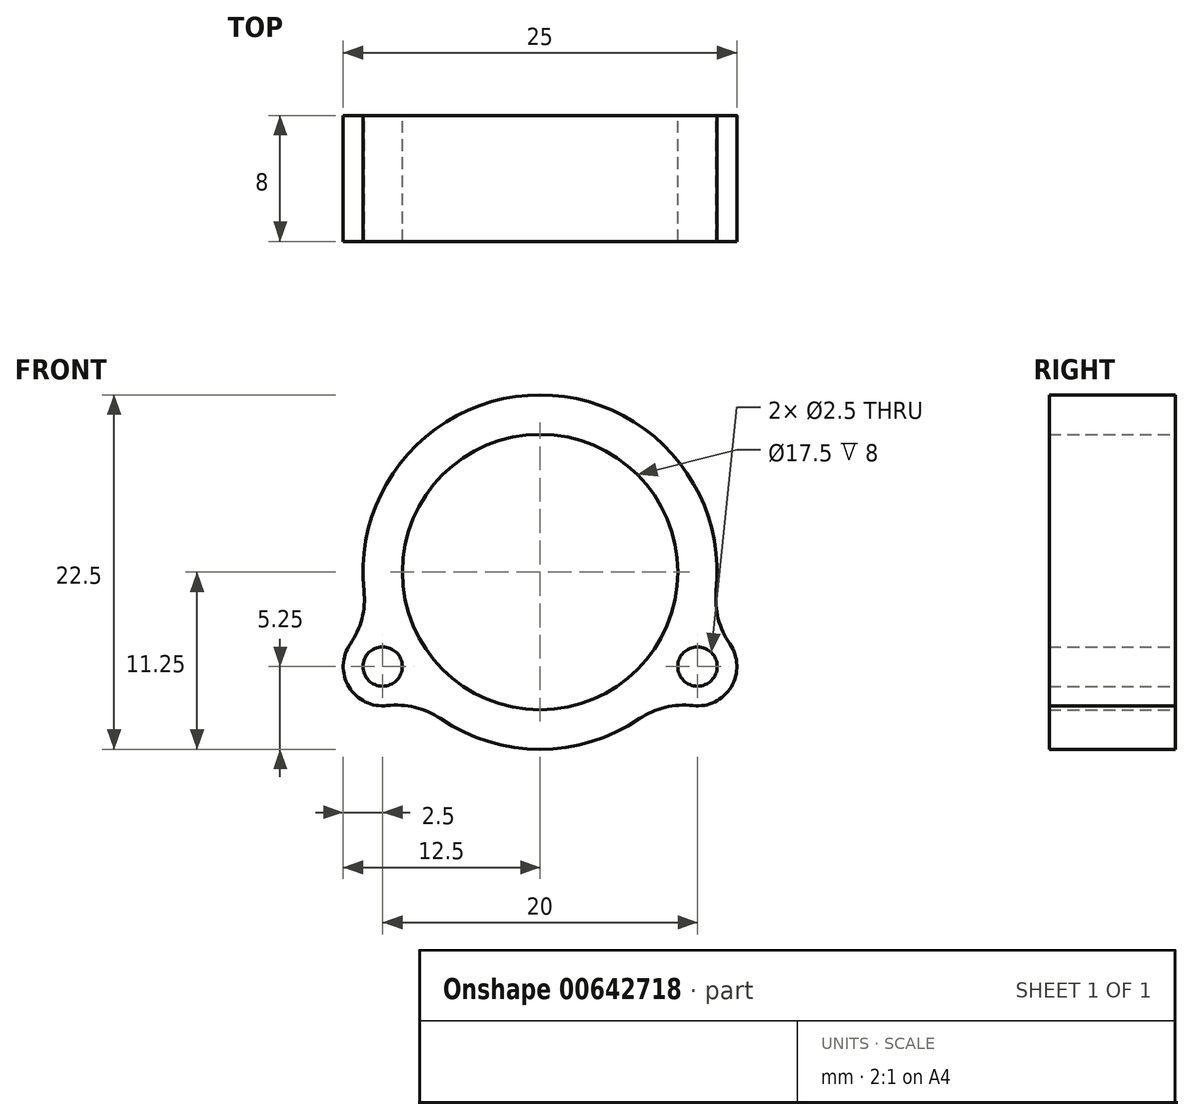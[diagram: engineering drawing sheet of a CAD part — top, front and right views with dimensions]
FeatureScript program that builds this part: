
annotation { "Feature Type Name" : "Feature", "Feature Type Description" : "" }
export const myFeature = defineFeature(function(context is Context, id is Id, definition is map)
    precondition{}
    {
        {
            var Q0;
            Q0=qCreatedBy(makeId("Front.planeOp"),FACE);
            var sketch = newSketch(context, id + "F0", { "sketchPlane" : qUnion([Q0])});
            skCircle(sketch, "E0", {"center": v(0, 0) * mm, "radius": 8.75 * mm});
            skArc(sketch, "E1", {"start": v(9.7, -8.48) * mm, "mid": v(12.14, -7.29) * mm, "end": v(12.05, -4.57) * mm});
            skArc(sketch, "E2", {"start": v(-12.05, -4.57) * mm, "mid": v(-12.14, -7.29) * mm, "end": v(-9.7, -8.48) * mm});
            skPoint(sketch, "E3.orphan", {"position": v(9, -6) * mm});
            skPoint(sketch, "E4.orphan", {"position": v(-11.68, -0.75) * mm});
            skPoint(sketch, "E5.start.orphan", {"position": v(-6.37, -6) * mm});
            skArc(sketch, "E6.trimOffspring", {"start": v(-6.31, -9.31) * mm, "mid": v(0, -11.25) * mm, "end": v(6.31, -9.31) * mm});
            skArc(sketch, "E7.trimOffspring", {"start": v(11.19, -1.2) * mm, "mid": v(0, 11.25) * mm, "end": v(-11.19, -1.2) * mm});
            skCircle(sketch, "E8", {"center": v(-10, -6) * mm, "radius": 1.25 * mm});
            skCircle(sketch, "E9", {"center": v(10, -6) * mm, "radius": 1.25 * mm});
            skPoint(sketch, "E10.visualSharp", {"position": v(10.66, -3.59) * mm});
            skArc(sketch, "E10.filletArc", {"start": v(11.19, -1.2) * mm, "mid": v(11.31, -2.96) * mm, "end": v(12.05, -4.57) * mm});
            skPoint(sketch, "E11.visualSharp", {"position": v(8.18, -7.72) * mm});
            skArc(sketch, "E11.filletArc", {"start": v(9.7, -8.48) * mm, "mid": v(7.94, -8.6) * mm, "end": v(6.31, -9.31) * mm});
            skPoint(sketch, "E12.visualSharp", {"position": v(-10.66, -3.59) * mm});
            skArc(sketch, "E12.filletArc", {"start": v(-12.05, -4.57) * mm, "mid": v(-11.31, -2.96) * mm, "end": v(-11.19, -1.2) * mm});
            skPoint(sketch, "E13.visualSharp", {"position": v(-8.18, -7.72) * mm});
            skArc(sketch, "E13.filletArc", {"start": v(-6.31, -9.31) * mm, "mid": v(-7.94, -8.6) * mm, "end": v(-9.7, -8.48) * mm});
            skSolve(sketch);
        }
        {
            var Q0;
            Q0=makeQuery(id+"F0.imprint","IMPRINT",FACE,{"disambiguationData":[TD([[makeQuery(id+"F0.imprint","IMPRINT",EDGE,{"derivedFrom":sQuery(id+"F0.wireOp",EDGE,"E0")}),-1.0]])]});
            extrude(context, id + "F1", {"entities" : qUnion([Q0]), "depth" : 8 * mm, "offsetDistance" : 25 * mm});
        }
    });
